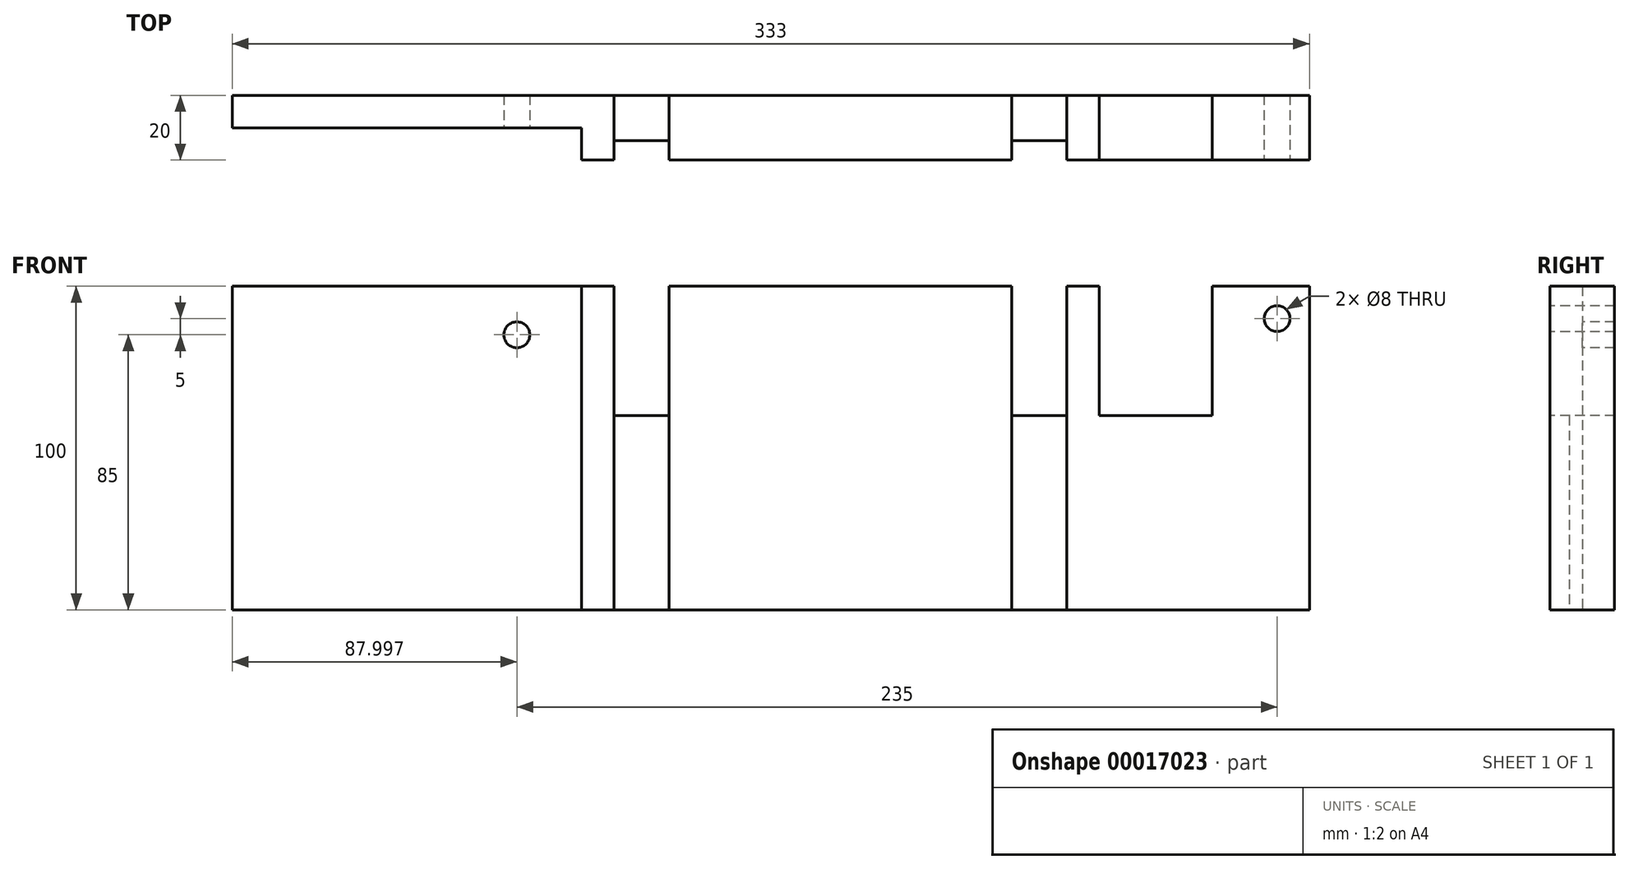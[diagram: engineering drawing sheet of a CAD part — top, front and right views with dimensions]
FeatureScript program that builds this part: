
annotation { "Feature Type Name" : "Feature", "Feature Type Description" : "" }
export const myFeature = defineFeature(function(context is Context, id is Id, definition is map)
    precondition{}
    {
        {
            var Q0;
            Q0=qCreatedBy(makeId("Front.planeOp"),FACE);
            var sketch = newSketch(context, id + "F0", { "sketchPlane" : qUnion([Q0])});
            skLineSegment(sketch, "E0.bottom", {"start": v(153.73, 100) * mm, "end": v(-196.27, 100) * mm});
            skLineSegment(sketch, "E0.top", {"start": v(153.73, 0) * mm, "end": v(-196.27, 0) * mm});
            skLineSegment(sketch, "E0.left", {"start": v(153.73, 100) * mm, "end": v(153.73, 0) * mm});
            skLineSegment(sketch, "E0.right", {"start": v(-196.27, 100) * mm, "end": v(-196.27, 0) * mm});
            skSolve(sketch);
        }
        {
            var Q0;
            Q0=makeQuery(id+"F0.imprint","IMPRINT",FACE,{"disambiguationData":[TD([[makeQuery(id+"F0.imprint","IMPRINT",EDGE,{"derivedFrom":sQuery(id+"F0.wireOp",EDGE,"E0.bottom")}),1.0]])]});
            extrude(context, id + "F1", {"entities" : qUnion([Q0]), "depth" : 20 * mm});
        }
        {
            var Q0;
            Q0=makeQuery(id+"F1.opExtrude","CAP_FACE",FACE,{"disambiguationData":[OSD([sQuery(id+"F0.wireOp",EDGE,"E0.bottom"),sQuery(id+"F0.wireOp",EDGE,"E0.top"),sQuery(id+"F0.wireOp",EDGE,"E0.left"),sQuery(id+"F0.wireOp",EDGE,"E0.right")])],"isStart":false});
            var sketch = newSketch(context, id + "F2", { "sketchPlane" : qUnion([Q0])});
            skLineSegment(sketch, "E1.bottom", {"start": v(-196.27, 100) * mm, "end": v(-71.27, 100) * mm});
            skLineSegment(sketch, "E1.top", {"start": v(-196.27, 0) * mm, "end": v(-71.27, 0) * mm});
            skLineSegment(sketch, "E1.left", {"start": v(-196.27, 100) * mm, "end": v(-196.27, 0) * mm});
            skLineSegment(sketch, "E1.right", {"start": v(-71.27, 100) * mm, "end": v(-71.27, 0) * mm});
            skSolve(sketch);
        }
        {
            var Q0;
            Q0 = qSketchRegion(id + "F2", true);
            extrude(context, id + "F3", {"entities" : qUnion([Q0]), "operationType" : NewBodyOperationType.REMOVE, "oppositeDirection" : true, "depth" : 10 * mm});
        }
        {
            var Q0;
            Q0=makeQuery(id+"F1.opExtrude","CAP_FACE",FACE,{"disambiguationData":[OSD([sQuery(id+"F0.wireOp",EDGE,"E0.bottom"),sQuery(id+"F0.wireOp",EDGE,"E0.top"),sQuery(id+"F0.wireOp",EDGE,"E0.left"),sQuery(id+"F0.wireOp",EDGE,"E0.right")])],"isStart":false});
            var sketch = newSketch(context, id + "F4", { "sketchPlane" : qUnion([Q0])});
            skCircle(sketch, "E2", {"center": v(143.73, 90) * mm, "radius": 4 * mm});
            skCircle(sketch, "E3", {"center": v(-91.27, 85) * mm, "radius": 4 * mm});
            skSolve(sketch);
        }
        {
            var Q0;
            Q0 = qSketchRegion(id + "F4", true);
            extrude(context, id + "F5", {"entities" : qUnion([Q0]), "operationType" : NewBodyOperationType.REMOVE, "endBound" : BoundingType.THROUGH_ALL, "oppositeDirection" : true, "depth" : 25 * mm});
        }
        {
            var Q0;
            Q0=makeQuery(id+"F1.opExtrude","CAP_FACE",FACE,{"disambiguationData":[OSD([sQuery(id+"F0.wireOp",EDGE,"E0.bottom"),sQuery(id+"F0.wireOp",EDGE,"E0.top"),sQuery(id+"F0.wireOp",EDGE,"E0.left"),sQuery(id+"F0.wireOp",EDGE,"E0.right")])],"isStart":false});
            var sketch = newSketch(context, id + "F6", { "sketchPlane" : qUnion([Q0])});
            skLineSegment(sketch, "E4.bottom", {"start": v(123.73, 100) * mm, "end": v(88.73, 100) * mm});
            skLineSegment(sketch, "E4.top", {"start": v(123.73, 60) * mm, "end": v(88.73, 60) * mm});
            skLineSegment(sketch, "E4.left", {"start": v(123.73, 100) * mm, "end": v(123.73, 60) * mm});
            skLineSegment(sketch, "E4.right", {"start": v(88.73, 100) * mm, "end": v(88.73, 60) * mm});
            skSolve(sketch);
        }
        {
            var Q0;
            Q0 = qSketchRegion(id + "F6", true);
            extrude(context, id + "F7", {"entities" : qUnion([Q0]), "operationType" : NewBodyOperationType.REMOVE, "endBound" : BoundingType.THROUGH_ALL, "oppositeDirection" : true, "depth" : 25 * mm});
        }
        {
            var Q0;
            Q0=makeQuery(id+"F1.opExtrude","CAP_FACE",FACE,{"disambiguationData":[OSD([sQuery(id+"F0.wireOp",EDGE,"E0.bottom"),sQuery(id+"F0.wireOp",EDGE,"E0.top"),sQuery(id+"F0.wireOp",EDGE,"E0.left"),sQuery(id+"F0.wireOp",EDGE,"E0.right")])],"isStart":false});
            var sketch = newSketch(context, id + "F8", { "sketchPlane" : qUnion([Q0])});
            skLineSegment(sketch, "E5.bottom", {"start": v(-61.27, 100) * mm, "end": v(-44.27, 100) * mm});
            skLineSegment(sketch, "E5.top", {"start": v(-61.27, 60) * mm, "end": v(-44.27, 60) * mm});
            skLineSegment(sketch, "E5.left", {"start": v(-61.27, 100) * mm, "end": v(-61.27, 60) * mm});
            skLineSegment(sketch, "E5.right", {"start": v(-44.27, 100) * mm, "end": v(-44.27, 60) * mm});
            skLineSegment(sketch, "E6.bottom", {"start": v(-179.27, 100.73) * mm, "end": v(-196.27, 100.73) * mm});
            skLineSegment(sketch, "E6.top", {"start": v(-179.27, -20) * mm, "end": v(-196.27, -20) * mm});
            skLineSegment(sketch, "E6.left", {"start": v(-179.27, 100.73) * mm, "end": v(-179.27, -20) * mm});
            skLineSegment(sketch, "E6.right", {"start": v(-196.27, 100.73) * mm, "end": v(-196.27, -20) * mm});
            skLineSegment(sketch, "E7.bottom", {"start": v(78.73, 100) * mm, "end": v(61.73, 100) * mm});
            skLineSegment(sketch, "E7.top", {"start": v(78.73, 60) * mm, "end": v(61.73, 60) * mm});
            skLineSegment(sketch, "E7.left", {"start": v(78.73, 100) * mm, "end": v(78.73, 60) * mm});
            skLineSegment(sketch, "E7.right", {"start": v(61.73, 100) * mm, "end": v(61.73, 60) * mm});
            skSolve(sketch);
        }
        {
            var Q0;
            Q0 = qSketchRegion(id + "F8", true);
            extrude(context, id + "F9", {"entities" : qUnion([Q0]), "operationType" : NewBodyOperationType.REMOVE, "endBound" : BoundingType.THROUGH_ALL, "oppositeDirection" : true, "depth" : 5 * mm});
        }
        {
            var Q0;
            Q0=makeQuery(id+"F1.opExtrude","CAP_FACE",FACE,{"disambiguationData":[OSD([sQuery(id+"F0.wireOp",EDGE,"E0.bottom"),sQuery(id+"F0.wireOp",EDGE,"E0.top"),sQuery(id+"F0.wireOp",EDGE,"E0.left"),sQuery(id+"F0.wireOp",EDGE,"E0.right")])],"isStart":false});
            var sketch = newSketch(context, id + "F10", { "sketchPlane" : qUnion([Q0])});
            skLineSegment(sketch, "E8.bottom", {"start": v(-61.27, 60) * mm, "end": v(-44.27, 60) * mm});
            skLineSegment(sketch, "E8.top", {"start": v(-61.27, 0) * mm, "end": v(-44.27, 0) * mm});
            skLineSegment(sketch, "E8.left", {"start": v(-61.27, 60) * mm, "end": v(-61.27, 0) * mm});
            skLineSegment(sketch, "E8.right", {"start": v(-44.27, 60) * mm, "end": v(-44.27, 0) * mm});
            skLineSegment(sketch, "E9.bottom", {"start": v(61.73, 60) * mm, "end": v(78.73, 60) * mm});
            skLineSegment(sketch, "E9.top", {"start": v(61.73, 0) * mm, "end": v(78.73, 0) * mm});
            skLineSegment(sketch, "E9.left", {"start": v(61.73, 60) * mm, "end": v(61.73, 0) * mm});
            skLineSegment(sketch, "E9.right", {"start": v(78.73, 60) * mm, "end": v(78.73, 0) * mm});
            skSolve(sketch);
        }
        {
            var Q0;
            Q0 = qSketchRegion(id + "F10", true);
            extrude(context, id + "F11", {"entities" : qUnion([Q0]), "operationType" : NewBodyOperationType.REMOVE, "oppositeDirection" : true, "depth" : 6 * mm});
        }
    });
